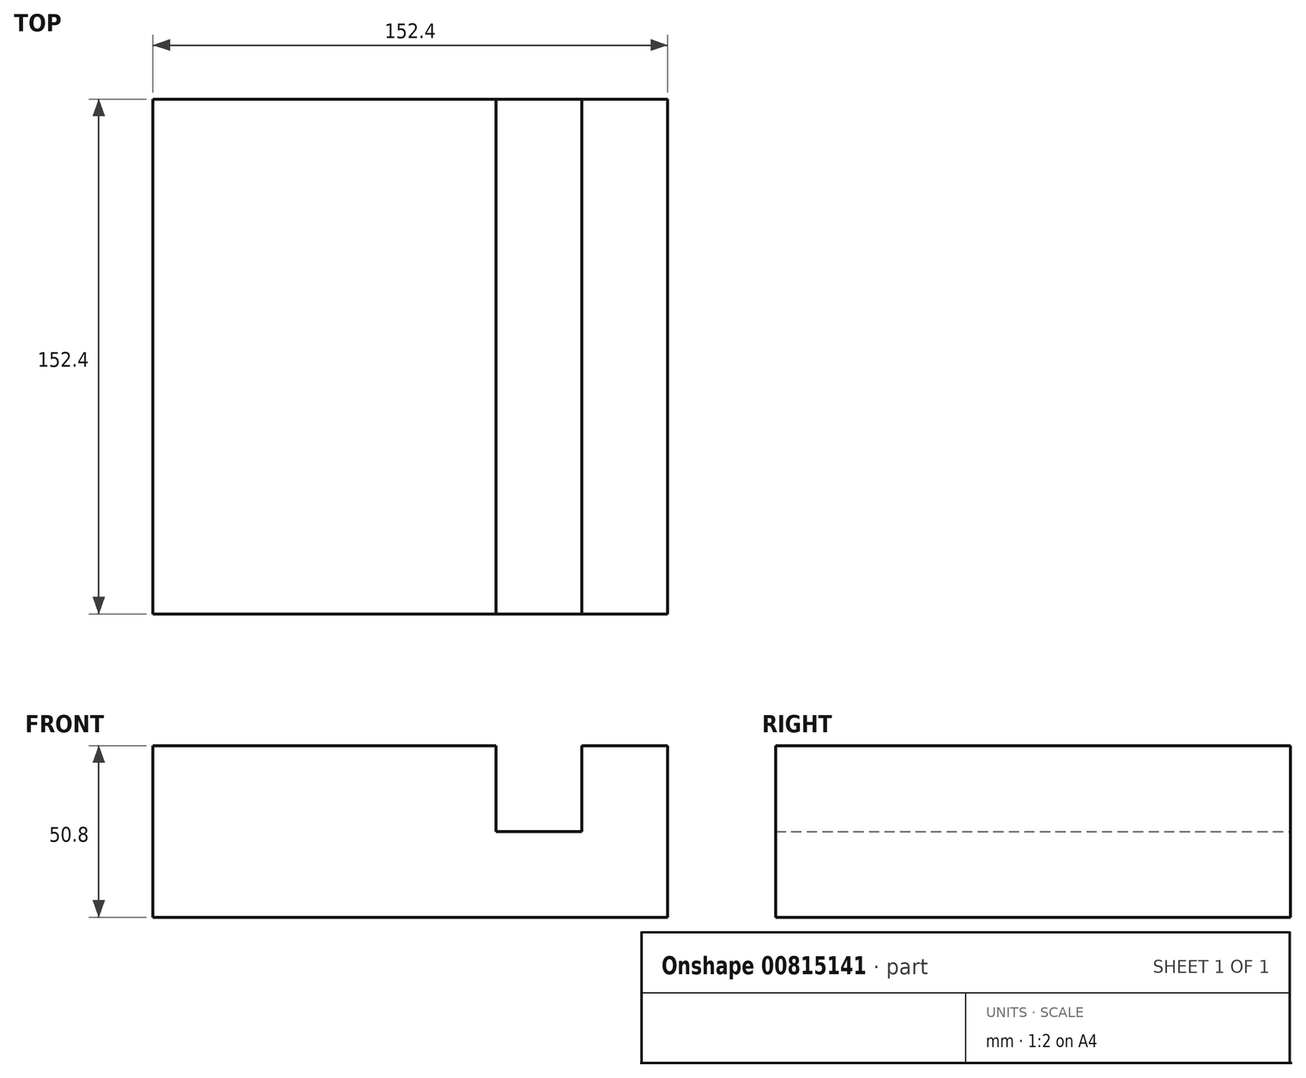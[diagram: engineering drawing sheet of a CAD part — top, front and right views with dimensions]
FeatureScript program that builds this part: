
annotation { "Feature Type Name" : "Feature", "Feature Type Description" : "" }
export const myFeature = defineFeature(function(context is Context, id is Id, definition is map)
    precondition{}
    {
        {
            var Q0;
            Q0=qCreatedBy(makeId("Front.planeOp"),FACE);
            var sketch = newSketch(context, id + "F0", { "sketchPlane" : qUnion([Q0])});
            skLineSegment(sketch, "E0", {"start": v(0, 0) * mm, "end": v(0, 50.8) * mm});
            skLineSegment(sketch, "E1", {"start": v(0, 50.8) * mm, "end": v(101.6, 50.8) * mm});
            skLineSegment(sketch, "E2", {"start": v(101.6, 50.8) * mm, "end": v(101.6, 25.4) * mm});
            skLineSegment(sketch, "E3", {"start": v(101.6, 25.4) * mm, "end": v(127, 25.4) * mm});
            skLineSegment(sketch, "E4", {"start": v(127, 25.4) * mm, "end": v(127, 50.8) * mm});
            skLineSegment(sketch, "E5", {"start": v(127, 50.8) * mm, "end": v(152.4, 50.8) * mm});
            skLineSegment(sketch, "E6", {"start": v(152.4, 50.8) * mm, "end": v(152.4, 0) * mm});
            skLineSegment(sketch, "E7", {"start": v(0, 0) * mm, "end": v(152.4, 0) * mm});
            skSolve(sketch);
        }
        {
            var Q0;
            Q0 = qSketchRegion(id + "F0", true);
            extrude(context, id + "F1", {"entities" : qUnion([Q0]), "depth" : 152.4 * mm, "offsetDistance" : 25.4 * mm});
        }
    });
